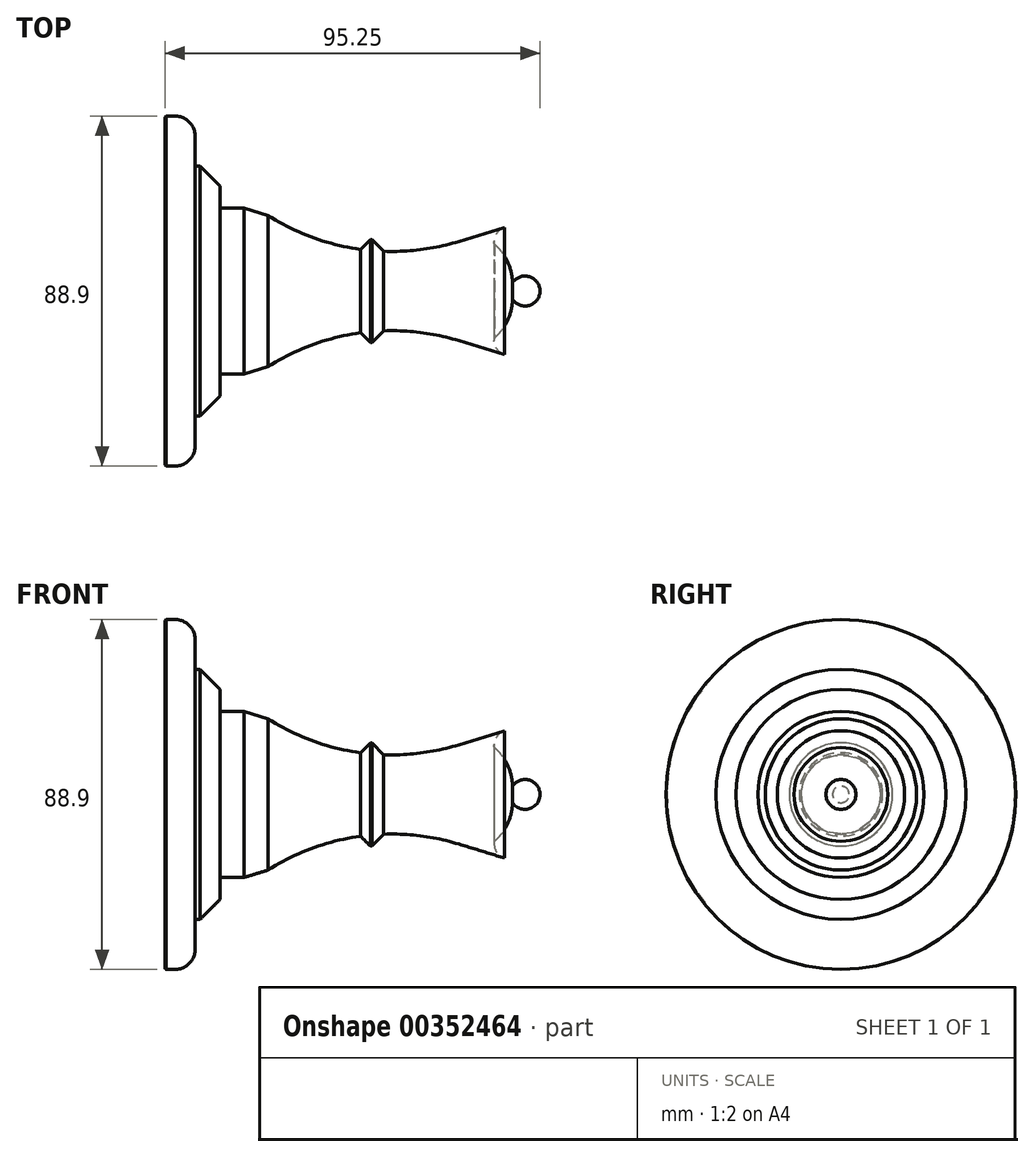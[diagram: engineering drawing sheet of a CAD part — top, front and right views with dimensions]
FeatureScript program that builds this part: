
annotation { "Feature Type Name" : "Feature", "Feature Type Description" : "" }
export const myFeature = defineFeature(function(context is Context, id is Id, definition is map)
    precondition{}
    {
        {
            var Q0;
            Q0=qCreatedBy(makeId("Front.planeOp"),FACE);
            var sketch = newSketch(context, id + "F0", { "sketchPlane" : qUnion([Q0])});
            skArc(sketch, "E0", {"start": v(0, 0) * mm, "mid": v(-2.7, 3.65) * mm, "end": v(-6.98, 2.1) * mm});
            skArc(sketch, "E1", {"start": v(-6.98, 2.1) * mm, "mid": v(-8.26, 7.5) * mm, "end": v(-11.6, 11.92) * mm});
            skLineSegment(sketch, "E2", {"start": v(-8.96, 16.18) * mm, "end": v(-20.62, 12.62) * mm});
            skArc(sketch, "E3", {"start": v(-8.96, 16.18) * mm, "mid": v(-11.09, 14.55) * mm, "end": v(-11.6, 11.92) * mm});
            skLineSegment(sketch, "E4", {"start": v(0, 0) * mm, "end": v(-95.25, 0) * mm});
            skLineSegment(sketch, "E5", {"start": v(-95.25, 0) * mm, "end": v(-95.25, 44.45) * mm});
            skLineSegment(sketch, "E6", {"start": v(-95.25, 44.45) * mm, "end": v(-87.63, 44.45) * mm});
            skLineSegment(sketch, "E7", {"start": v(-87.63, 44.45) * mm, "end": v(-87.63, 31.75) * mm});
            skLineSegment(sketch, "E8", {"start": v(-87.63, 31.75) * mm, "end": v(-81.28, 31.75) * mm});
            skLineSegment(sketch, "E9", {"start": v(-75.18, 21.08) * mm, "end": v(-69.11, 19.23) * mm});
            skArc(sketch, "E10", {"start": v(-69.11, 19.23) * mm, "mid": v(-57.82, 13.64) * mm, "end": v(-45.6, 10.6) * mm});
            skLineSegment(sketch, "E11", {"start": v(-45.6, 10.6) * mm, "end": v(-42.9, 13.3) * mm});
            skLineSegment(sketch, "E12", {"start": v(-42.9, 13.3) * mm, "end": v(-39.71, 10.1) * mm});
            skPoint(sketch, "E13.end.orphan", {"position": v(-81.28, 19.23) * mm});
            skLineSegment(sketch, "E14", {"start": v(-75.18, 21.08) * mm, "end": v(-81.28, 21.08) * mm});
            skLineSegment(sketch, "E15", {"start": v(-81.28, 21.08) * mm, "end": v(-81.28, 31.75) * mm});
            skArc(sketch, "E16.trimOffspring", {"start": v(-39.71, 10.1) * mm, "mid": v(-30.06, 10.57) * mm, "end": v(-20.62, 12.62) * mm});
            skSolve(sketch);
        }
        {
            var Q0;
            Q0=makeQuery(id+"F0.imprint","IMPRINT",FACE,{"disambiguationData":[TD([[makeQuery(id+"F0.imprint","IMPRINT",EDGE,{"derivedFrom":sQuery(id+"F0.wireOp",EDGE,"E0")}),1.0]])]});
            var Q1;
            Q1=sQuery(id+"F0.wireOp",EDGE,"E4");
            revolve(context, id + "F1", {"entities" : qUnion([Q0]), "axis" : qUnion([Q1]), "revolveType" : RevolveType.FULL});
        }
        {
            var Q0;
            Q0=makeQuery(id+"F1.opRevolve","SWEPT_EDGE",EDGE,{"disambiguationData":[OSD([sQuery(id+"F0.wireOp",EDGE,"E6"),sQuery(id+"F0.wireOp",EDGE,"E7")])]});
            fillet(context, id + "F2", {"entities" : qUnion([Q0]), "radius" : 5.08 * mm, "tangentPropagation" : true, "allowEdgeOverflow" : false});
        }
        {
            var Q0;
            Q0=makeQuery(id+"F1.opRevolve","SWEPT_EDGE",EDGE,{"disambiguationData":[OSD([sQuery(id+"F0.wireOp",EDGE,"E8"),sQuery(id+"F0.wireOp",EDGE,"E15")])]});
            chamfer(context, id + "F3", {"entities" : qUnion([Q0]), "width" : 5.08 * mm, "tangentPropagation" : true});
        }
        {
            var Q0;
            Q0=makeQuery(id+"F1.opRevolve","SWEPT_EDGE",EDGE,{"disambiguationData":[OSD([sQuery(id+"F0.wireOp",EDGE,"E5"),sQuery(id+"F0.wireOp",EDGE,"E6")])]});
            var Q1;
            Q1=makeQuery(id+"F1.opRevolve","SWEPT_EDGE",EDGE,{"disambiguationData":[OSD([sQuery(id+"F0.wireOp",EDGE,"E11"),sQuery(id+"F0.wireOp",EDGE,"E12")])]});
            chamfer(context, id + "F4", {"entities" : qUnion([Q0, Q1]), "width" : 0.25 * mm, "tangentPropagation" : true});
        }
    });
